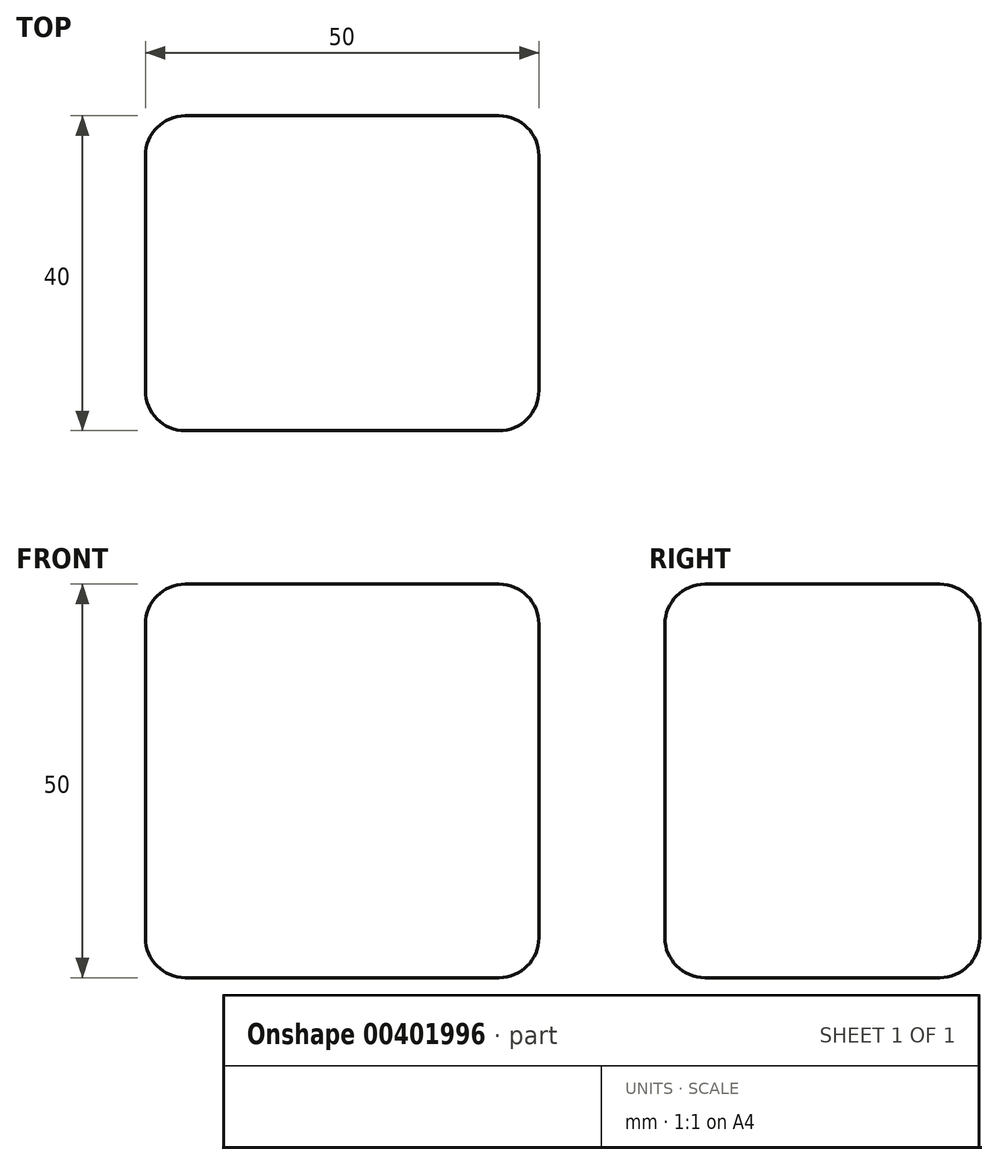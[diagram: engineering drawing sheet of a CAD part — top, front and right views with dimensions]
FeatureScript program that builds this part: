
annotation { "Feature Type Name" : "Feature", "Feature Type Description" : "" }
export const myFeature = defineFeature(function(context is Context, id is Id, definition is map)
    precondition{}
    {
        {
            var Q0;
            Q0=qCreatedBy(makeId("Top.planeOp"),FACE);
            var sketch = newSketch(context, id + "F0", { "sketchPlane" : qUnion([Q0])});
            skLineSegment(sketch, "E0.bottom", {"start": v(-25, 20) * mm, "end": v(25, 20) * mm});
            skLineSegment(sketch, "E0.top", {"start": v(-25, -20) * mm, "end": v(25, -20) * mm});
            skLineSegment(sketch, "E0.left", {"start": v(-25, 20) * mm, "end": v(-25, -20) * mm});
            skLineSegment(sketch, "E0.right", {"start": v(25, 20) * mm, "end": v(25, -20) * mm});
            skPoint(sketch, "E0.middle", {"position": v(0, 0) * mm});
            skSolve(sketch);
        }
        {
            var Q0;
            Q0 = qSketchRegion(id + "F0", true);
            extrude(context, id + "F1", {"entities" : qUnion([Q0]), "depth" : 50 * mm});
        }
        {
            var Q0;
            Q0=makeQuery(id+"F1.opExtrude","CAP_EDGE",EDGE,{"disambiguationData":[OSD([sQuery(id+"F0.wireOp",EDGE,"E0.bottom")])],"isStart":false});
            var Q1;
            Q1=makeQuery(id+"F1.opExtrude","CAP_EDGE",EDGE,{"disambiguationData":[OSD([sQuery(id+"F0.wireOp",EDGE,"E0.left")])],"isStart":false});
            var Q2;
            Q2=makeQuery(id+"F1.opExtrude","CAP_EDGE",EDGE,{"disambiguationData":[OSD([sQuery(id+"F0.wireOp",EDGE,"E0.right")])],"isStart":false});
            var Q3;
            Q3=makeQuery(id+"F1.opExtrude","CAP_EDGE",EDGE,{"disambiguationData":[OSD([sQuery(id+"F0.wireOp",EDGE,"E0.top")])],"isStart":false});
            var Q4;
            Q4=makeQuery(id+"F1.opExtrude","SWEPT_EDGE",EDGE,{"disambiguationData":[OSD([sQuery(id+"F0.wireOp",EDGE,"E0.top"),sQuery(id+"F0.wireOp",EDGE,"E0.right")])]});
            var Q5;
            Q5=makeQuery(id+"F1.opExtrude","CAP_EDGE",EDGE,{"disambiguationData":[OSD([sQuery(id+"F0.wireOp",EDGE,"E0.top")])],"isStart":true});
            var Q6;
            Q6=makeQuery(id+"F1.opExtrude","SWEPT_EDGE",EDGE,{"disambiguationData":[OSD([sQuery(id+"F0.wireOp",EDGE,"E0.top"),sQuery(id+"F0.wireOp",EDGE,"E0.left")])]});
            var Q7;
            Q7=makeQuery(id+"F1.opExtrude","CAP_EDGE",EDGE,{"disambiguationData":[OSD([sQuery(id+"F0.wireOp",EDGE,"E0.left")])],"isStart":true});
            var Q8;
            Q8=makeQuery(id+"F1.opExtrude","SWEPT_EDGE",EDGE,{"disambiguationData":[OSD([sQuery(id+"F0.wireOp",EDGE,"E0.bottom"),sQuery(id+"F0.wireOp",EDGE,"E0.left")])]});
            var Q9;
            Q9=makeQuery(id+"F1.opExtrude","CAP_EDGE",EDGE,{"disambiguationData":[OSD([sQuery(id+"F0.wireOp",EDGE,"E0.bottom")])],"isStart":true});
            var Q10;
            Q10=makeQuery(id+"F1.opExtrude","CAP_EDGE",EDGE,{"disambiguationData":[OSD([sQuery(id+"F0.wireOp",EDGE,"E0.right")])],"isStart":true});
            var Q11;
            Q11=makeQuery(id+"F1.opExtrude","SWEPT_EDGE",EDGE,{"disambiguationData":[OSD([sQuery(id+"F0.wireOp",EDGE,"E0.bottom"),sQuery(id+"F0.wireOp",EDGE,"E0.right")])]});
            fillet(context, id + "F2", {"entities" : qUnion([Q0, Q1, Q2, Q3, Q4, Q5, Q6, Q7, Q8, Q9, Q10, Q11]), "radius" : 5.08 * mm, "tangentPropagation" : true, "allowEdgeOverflow" : false});
        }
    });
